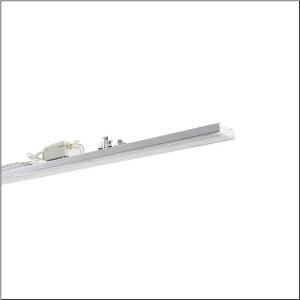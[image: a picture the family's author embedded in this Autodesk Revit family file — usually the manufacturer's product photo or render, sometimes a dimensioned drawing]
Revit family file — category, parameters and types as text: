
# Revit family: licross_21_recessed_mo_52tl12dv4dxg
name_source: partatom
category: Lighting Fixtures
units: mm (PartAtom-declared; Revit-internal decimal feet)

## family parameters
Cut with Voids When Loaded = No
Host = Face
Light Source = No
Part Type = Normal
Room Calculation Point = No
Round Connector Dimension = Use Diameter
Shared = No

## types (1)
- --- (1 x LED, 13000 lm, 71 W, 4000K)
    Apparent Load = 71 VA
    CIE Flux Codes = 72 92 99 100 100
    Color Rendering = 80
    Color Temperature = 4000K
    Default Elevation = 1800 mm
    Description = Licross 21 Recessed MO, luminaire insert, of sheet steel, galvanised, coil coated, white, length: 2.250mm, width: 66mm, height: 67mm, LED rated luminous flux: 13.000lm, light colour: 840, SDCM (Standard Deviation of Colour Matching)MacAdam ≤ 3 SDCM (initial), control gear: DALI 2, with plug, 5-pole, with phase selection, mains connection: 220..240V, AC, 50/60Hz, rated input power: 71W, internal wiring halogen-free, primary optical cover: cover, of PMMA, light emission: direct distribution, primary light characteristic: symmetric, protection rating (complete): IP40, insulation class (complete): insulation class I (protective earthing), certification: CE, ENEC, VDE, UKCA, protection symbol: D if used in an environment without relevant dust loads with corresponding accessories, impact resistance: IK06, permissible ambient temperature for indoor applications: -25..+35°C, corresponds to IFS (International Featured Standards) requirements for safety and quality in the food industry, reducing of maximum allowable ambient temperature of 5°C with ceiling mounting, LABS conformity tested according to VDMA 24364:2018-05, The light source and the operating device comply with the requirements of the Ecodesign Regulation (EU) 2019/2020 and are replaceable in accordance with this regulation, packaging unit: 1 piece
    Height = 58 mm
    Lamp = 1 x LED
    Lamp Light Flux = 13000 lm
    Lamp Power = 71 W
    Lamp count = 1
    Length = 2250 mm
    Luminous efficacy = 183 lm/W
    Manufacturer = Siteco
    ModVariant = No
    Model = 52TL12DV4DXG
    Mounting Place = Ceiling
    Mounting Type = Pendant
    Number of Poles = 1
    OnlyDefault = Yes
    Power Factor = 1
    Product Name = Licross 21 Recessed MO
    Product group = luminaire insert | ceiling pendant
    ProductGroupID = 901
    Protection Class = Protection class I
    Protection Degree = IP 40
    RLX_Detail_Level = 1
    RLX_Emergency_Light_Flux = 0 lm
    RLX_Emergency_Type = 0
    RLX_Emergency_Type_DB = No
    RlxData = <blob elided: 29993 chars, md5=539156a9>
    Socket = socket
    Standby Power = 0 W
    System Light Flux = 13000 lm
    System Power = 71 W
    Type Comments = factory setting: luminous flux: 100 % | dim-lin: 254 | 324 mA
    Type Image = l_1296930.jpg
    URL = http://relux.com
    VarID = @adj_128177
    Voltage = 0 V
    Weight = 0.00 kg
    Width = 66 mm

## geometry (parser evidence)
native form markers: Blend x4, Sweep x10
no freeform markers — native parametric forms only
